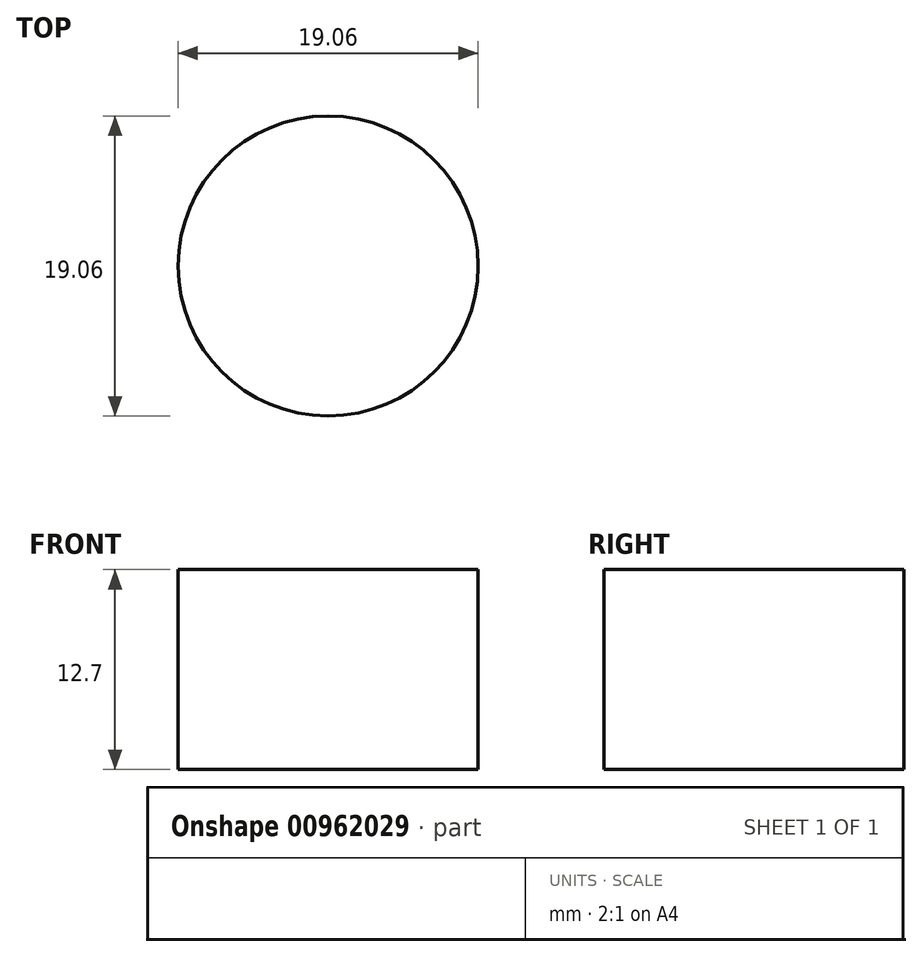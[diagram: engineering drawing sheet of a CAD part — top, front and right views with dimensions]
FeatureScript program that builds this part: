
annotation { "Feature Type Name" : "Feature", "Feature Type Description" : "" }
export const myFeature = defineFeature(function(context is Context, id is Id, definition is map)
    precondition{}
    {
        {
            var Q0;
            Q0=qCreatedBy(makeId("Top.planeOp"),FACE);
            var sketch = newSketch(context, id + "F0", { "sketchPlane" : qUnion([Q0])});
            skCircle(sketch, "E0", {"center": v(0, 0) * mm, "radius": 9.53 * mm});
            skSolve(sketch);
        }
        {
            var Q0;
            Q0=makeQuery(id+"F0.imprint","IMPRINT",FACE,{"disambiguationData":[TD([[makeQuery(id+"F0.imprint","IMPRINT",EDGE,{"derivedFrom":sQuery(id+"F0.wireOp",EDGE,"E0")}),1.0]])]});
            extrude(context, id + "F1", {"entities" : qUnion([Q0]), "endBound" : BoundingType.SYMMETRIC, "depth" : 12.7 * mm, "offsetDistance" : 25.4 * mm});
        }
    });
